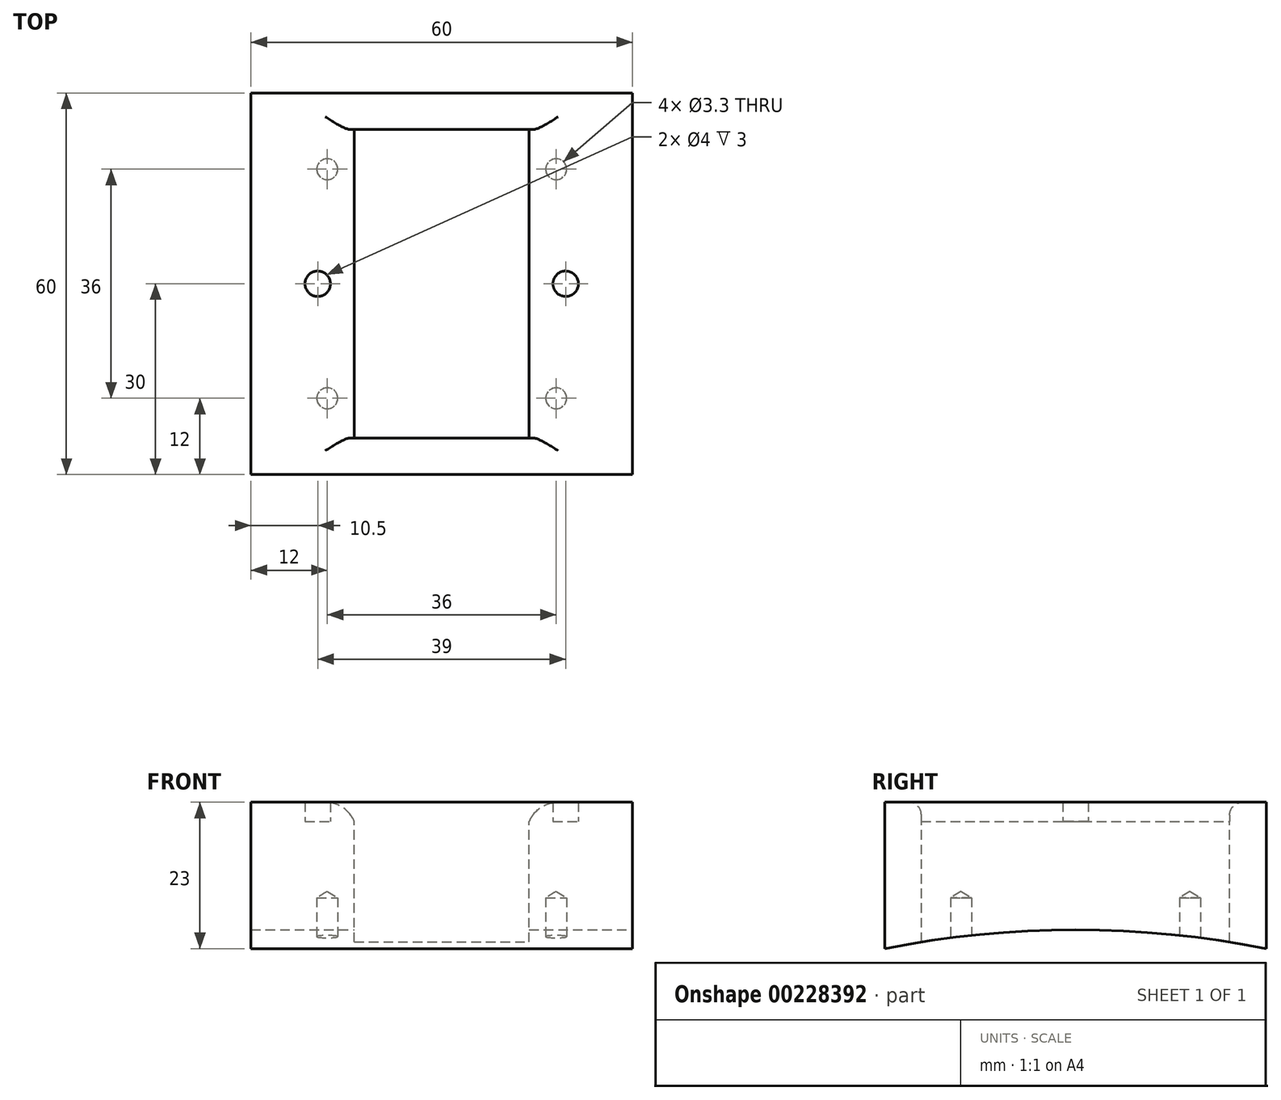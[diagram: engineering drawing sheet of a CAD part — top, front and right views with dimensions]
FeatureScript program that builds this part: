
annotation { "Feature Type Name" : "Feature", "Feature Type Description" : "" }
export const myFeature = defineFeature(function(context is Context, id is Id, definition is map)
    precondition{}
    {
        {
            var Q0;
            Q0=qCreatedBy(makeId("Top.planeOp"),FACE);
            var sketch = newSketch(context, id + "F0", { "sketchPlane" : qUnion([Q0])});
            skLineSegment(sketch, "E0.bottom", {"start": v(0, 0) * mm, "end": v(-27.5, 0) * mm});
            skLineSegment(sketch, "E0.top", {"start": v(0, 48.5) * mm, "end": v(-27.5, 48.5) * mm});
            skLineSegment(sketch, "E0.left", {"start": v(0, 0) * mm, "end": v(0, 48.5) * mm});
            skLineSegment(sketch, "E0.right", {"start": v(-27.5, 0) * mm, "end": v(-27.5, 48.5) * mm});
            skLineSegment(sketch, "E1.bottom", {"start": v(-43.75, 54.25) * mm, "end": v(16.25, 54.25) * mm});
            skLineSegment(sketch, "E1.top", {"start": v(-43.75, -5.75) * mm, "end": v(16.25, -5.75) * mm});
            skLineSegment(sketch, "E1.left", {"start": v(-43.75, 54.25) * mm, "end": v(-43.75, -5.75) * mm});
            skLineSegment(sketch, "E1.right", {"start": v(16.25, 54.25) * mm, "end": v(16.25, -5.75) * mm});
            skLineSegment(sketch, "E2", {"start": v(-27.5, 24.25) * mm, "end": v(0, 24.25) * mm, "construction": true});
            skLineSegment(sketch, "E3", {"start": v(-13.75, 48.5) * mm, "end": v(-13.75, 0) * mm, "construction": true});
            skPoint(sketch, "E4", {"position": v(-13.75, 24.25) * mm});
            skPoint(sketch, "E5", {"position": v(-33.25, 24.25) * mm});
            skPoint(sketch, "E6.MirrorP", {"position": v(5.75, 24.25) * mm});
            skPoint(sketch, "E7", {"position": v(-43.75, 24.25) * mm});
            skPoint(sketch, "E8", {"position": v(-13.75, 54.25) * mm});
            skLineSegment(sketch, "E9", {"start": v(-27.5, 24.25) * mm, "end": v(-59.54, 24.25) * mm, "construction": true});
            skLineSegment(sketch, "E10", {"start": v(-13.75, 48.5) * mm, "end": v(-13.75, 71.4) * mm, "construction": true});
            skSolve(sketch);
        }
        {
            var Q0;
            Q0=makeQuery(id+"F0.imprint","IMPRINT",FACE,{"disambiguationData":[TD([[makeQuery(id+"F0.imprint","IMPRINT",EDGE,{"derivedFrom":sQuery(id+"F0.wireOp",EDGE,"E0.bottom")}),1.0]])]});
            extrude(context, id + "F1", {"entities" : qUnion([Q0]), "depth" : 3 * mm});
        }
        {
            var Q0;
            Q0=sQuery(id+"F0.wireOp",VERTEX,"E5");
            var Q1;
            Q1=sQuery(id+"F0.wireOp",VERTEX,"E6.MirrorP");
            var Q2;
            Q2=sQuery(id+"F0.wireOp",VERTEX,"zkM92I10-sr8Q-tOJ8-xdno-DzMIJFy0W358.end");
            var Q3;
            Q3=sQuery(id+"F0.wireOp",VERTEX,"9b0ebf9e-f762-4fc6-b844-4a83bfaebebf0.MirrorCS.end");
            var Q4;
            Q4=makeQuery(id+"F1.opExtrude","SWEPT_BODY",BODY,{"disambiguationData":[OSD([sQuery(id+"F0.wireOp",EDGE,"E0.bottom"),sQuery(id+"F0.wireOp",EDGE,"E0.top"),sQuery(id+"F0.wireOp",EDGE,"E0.left"),sQuery(id+"F0.wireOp",EDGE,"E0.right"),sQuery(id+"F0.wireOp",EDGE,"llcFhKEJ-WzVQ-eruR-hBAQ-GDCpW0LM7jkg.bottom"),sQuery(id+"F0.wireOp",EDGE,"llcFhKEJ-WzVQ-eruR-hBAQ-GDCpW0LM7jkg.top"),sQuery(id+"F0.wireOp",EDGE,"llcFhKEJ-WzVQ-eruR-hBAQ-GDCpW0LM7jkg.left"),sQuery(id+"F0.wireOp",EDGE,"llcFhKEJ-WzVQ-eruR-hBAQ-GDCpW0LM7jkg.right"),sQuery(id+"F0.wireOp",EDGE,"E1.bottom"),sQuery(id+"F0.wireOp",EDGE,"E1.top"),sQuery(id+"F0.wireOp",EDGE,"E1.left"),sQuery(id+"F0.wireOp",EDGE,"E1.right")])]});
            hole(context, id + "F2", {"style" : HoleStyle.SIMPLE, "endStyle" : HoleEndStyle.THROUGH, "oppositeDirection" : true, "holeDiameter" : (4) * mm, "startFromSketch" : true, "locations" : qUnion([Q0, Q1, Q2, Q3]), "scope" : qUnion([Q4]), "tappedDepth" : 12 * mm, "tapClearance" : 3});
        }
        {
            var Q0;
            Q0=makeQuery(id+"F1.opExtrude","CAP_EDGE",EDGE,{"disambiguationData":[OSD([sQuery(id+"F0.wireOp",EDGE,"E0.top")])],"isStart":false});
            var Q1;
            Q1=makeQuery(id+"F1.opExtrude","CAP_EDGE",EDGE,{"disambiguationData":[OSD([sQuery(id+"F0.wireOp",EDGE,"E0.bottom")])],"isStart":false});
            fillet(context, id + "F3", {"entities" : qUnion([Q0, Q1]), "radius" : 2 * mm, "tangentPropagation" : true, "allowEdgeOverflow" : false});
        }
        {
            var Q0;
            Q0=makeQuery(id+"F1.opExtrude","CAP_EDGE",EDGE,{"disambiguationData":[OSD([sQuery(id+"F0.wireOp",EDGE,"E0.right")])],"isStart":false});
            var Q1;
            Q1=makeQuery(id+"F1.opExtrude","CAP_EDGE",EDGE,{"disambiguationData":[OSD([sQuery(id+"F0.wireOp",EDGE,"E0.left")])],"isStart":false});
            fillet(context, id + "F4", {"entities" : qUnion([Q0, Q1]), "radius" : 5 * mm, "tangentPropagation" : true, "allowEdgeOverflow" : false});
        }
        {
            var Q0;
            Q0=makeQuery(id+"F0.imprint","IMPRINT",FACE,{"disambiguationData":[TD([[makeQuery(id+"F0.imprint","IMPRINT",EDGE,{"derivedFrom":sQuery(id+"F0.wireOp",EDGE,"E0.bottom")}),1.0]])]});
            extrude(context, id + "F5", {"entities" : qUnion([Q0]), "operationType" : NewBodyOperationType.ADD, "oppositeDirection" : true, "depth" : 20 * mm});
        }
        {
            var Q0;
            Q0=makeQuery(id+"F5.opExtrude","CAP_FACE",FACE,{"disambiguationData":[OSD([sQuery(id+"F0.wireOp",EDGE,"E0.bottom"),sQuery(id+"F0.wireOp",EDGE,"E0.top"),sQuery(id+"F0.wireOp",EDGE,"E0.left"),sQuery(id+"F0.wireOp",EDGE,"E0.right"),sQuery(id+"F0.wireOp",EDGE,"E1.bottom"),sQuery(id+"F0.wireOp",EDGE,"E1.top"),sQuery(id+"F0.wireOp",EDGE,"E1.left"),sQuery(id+"F0.wireOp",EDGE,"E1.right")])],"isStart":false});
            var sketch = newSketch(context, id + "F6", { "sketchPlane" : qUnion([Q0])});
            skLineSegment(sketch, "E11.bottom", {"start": v(4.25, -6.25) * mm, "end": v(-31.75, -6.25) * mm, "construction": true});
            skLineSegment(sketch, "E11.top", {"start": v(4.25, -42.25) * mm, "end": v(-31.75, -42.25) * mm, "construction": true});
            skLineSegment(sketch, "E11.left", {"start": v(4.25, -6.25) * mm, "end": v(4.25, -42.25) * mm, "construction": true});
            skLineSegment(sketch, "E11.right", {"start": v(-31.75, -6.25) * mm, "end": v(-31.75, -42.25) * mm, "construction": true});
            skPoint(sketch, "E11.middle", {"position": v(-13.75, -24.25) * mm});
            skSolve(sketch);
        }
        {
            var Q0;
            Q0=sQuery(id+"F6.wireOp",VERTEX,"E11.bottom.end");
            var Q1;
            Q1=sQuery(id+"F6.wireOp",VERTEX,"E11.bottom.start");
            var Q2;
            Q2=sQuery(id+"F6.wireOp",VERTEX,"E11.top.start");
            var Q3;
            Q3=sQuery(id+"F6.wireOp",VERTEX,"E11.top.end");
            var Q4;
            Q4=makeQuery(id+"F1.opExtrude","SWEPT_BODY",BODY,{"disambiguationData":[OSD([sQuery(id+"F0.wireOp",EDGE,"E0.bottom"),sQuery(id+"F0.wireOp",EDGE,"E0.top"),sQuery(id+"F0.wireOp",EDGE,"E0.left"),sQuery(id+"F0.wireOp",EDGE,"E0.right"),sQuery(id+"F0.wireOp",EDGE,"E1.bottom"),sQuery(id+"F0.wireOp",EDGE,"E1.top"),sQuery(id+"F0.wireOp",EDGE,"E1.left"),sQuery(id+"F0.wireOp",EDGE,"E1.right")])]});
            hole(context, id + "F7", {"style" : HoleStyle.SIMPLE, "endStyle" : HoleEndStyle.BLIND, "standardTappedOrClearance" : lookupTablePath({ "standard" : "ISO", "fit" : "Normal", "size" : "M3", "type" : "Clearance" }), "standardBlindInLast" : lookupTablePath({ "fit" : "Standard", "standard" : "ISO", "size" : "M3", "type" : "Clearance" }), "holeDiameter" : 3.3 * mm, "holeDepth" : 8 * mm, "tappedDepth" : 12 * mm, "tapClearance" : 3, "startFromSketch" : true, "locations" : qUnion([Q0, Q1, Q2, Q3]), "scope" : qUnion([Q4])});
        }
        {
            var Q0;
            Q0=qCreatedBy(makeId("Right.planeOp"),FACE);
            var sketch = newSketch(context, id + "F8", { "sketchPlane" : qUnion([Q0])});
            skArc(sketch, "E12", {"start": v(54.25, -20) * mm, "mid": v(24.25, -17.06) * mm, "end": v(-5.75, -20) * mm});
            skLineSegment(sketch, "E13", {"start": v(-5.75, -20) * mm, "end": v(54.25, -20) * mm});
            skSolve(sketch);
        }
        {
            var Q0;
            Q0 = qSketchRegion(id + "F8", true);
            extrude(context, id + "F9", {"entities" : qUnion([Q0]), "operationType" : NewBodyOperationType.REMOVE, "oppositeDirection" : true, "depth" : 100 * mm, "hasSecondDirection" : true, "secondDirectionOppositeDirection" : false, "secondDirectionDepth" : 100 * mm});
        }
    });
